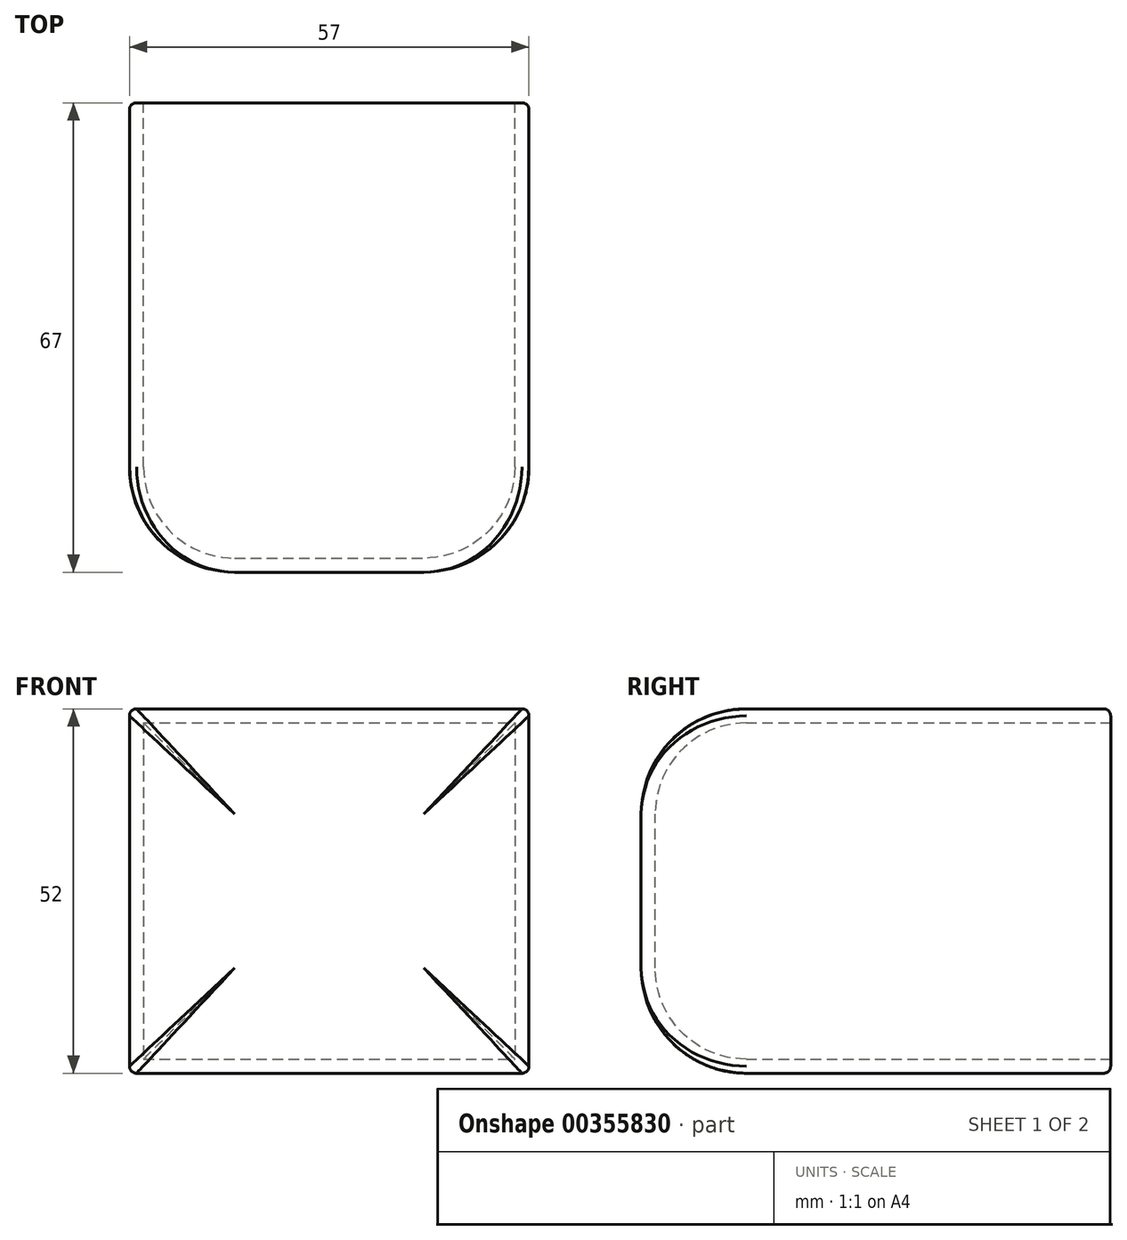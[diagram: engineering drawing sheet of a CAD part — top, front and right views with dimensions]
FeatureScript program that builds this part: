
annotation { "Feature Type Name" : "Feature", "Feature Type Description" : "" }
export const myFeature = defineFeature(function(context is Context, id is Id, definition is map)
    precondition{}
    {
        {
            var Q0;
            Q0=qCreatedBy(makeId("Front.planeOp"),FACE);
            var sketch = newSketch(context, id + "F0", { "sketchPlane" : qUnion([Q0])});
            skLineSegment(sketch, "E0.bottom", {"start": v(-28.5, 26) * mm, "end": v(28.5, 26) * mm});
            skLineSegment(sketch, "E0.top", {"start": v(-28.5, -26) * mm, "end": v(28.5, -26) * mm});
            skLineSegment(sketch, "E0.left", {"start": v(-28.5, 26) * mm, "end": v(-28.5, -26) * mm});
            skLineSegment(sketch, "E0.right", {"start": v(28.5, 26) * mm, "end": v(28.5, -26) * mm});
            skPoint(sketch, "E0.middle", {"position": v(0, 0) * mm});
            skSolve(sketch);
        }
        {
            var Q0;
            Q0=qSketchRegion(id+"F0",true);
            extrude(context, id + "F1", {"entities" : qUnion([Q0]), "depth" : 67 * mm});
        }
        {
            var Q0;
            Q0=makeQuery(id+"F1.opExtrude","CAP_FACE",FACE,{"disambiguationData":[OSD([sQuery(id+"F0.wireOp",EDGE,"E0.bottom"),sQuery(id+"F0.wireOp",EDGE,"E0.top"),sQuery(id+"F0.wireOp",EDGE,"E0.left"),sQuery(id+"F0.wireOp",EDGE,"E0.right")])],"isStart":false});
            fillet(context, id + "F2", {"entities" : qUnion([Q0]), "radius" : 15 * mm, "tangentPropagation" : true, "allowEdgeOverflow" : false});
        }
        {
            var Q0;
            Q0=makeQuery(id+"F1.opExtrude","CAP_FACE",FACE,{"disambiguationData":[OSD([sQuery(id+"F0.wireOp",EDGE,"E0.bottom"),sQuery(id+"F0.wireOp",EDGE,"E0.top"),sQuery(id+"F0.wireOp",EDGE,"E0.left"),sQuery(id+"F0.wireOp",EDGE,"E0.right")])],"isStart":true});
            shell(context, id + "F3", {"entities" : qUnion([Q0]), "thickness" : 2 * mm});
        }
        {
            var Q0;
            Q0=makeQuery(id+"F1.opExtrude","CAP_EDGE",EDGE,{"disambiguationData":[OSD([sQuery(id+"F0.wireOp",EDGE,"E0.left")])],"isStart":true});
            fillet(context, id + "F4", {"entities" : qUnion([Q0]), "radius" : 1 * mm, "tangentPropagation" : true, "allowEdgeOverflow" : false});
        }
        {
            var Q0;
            Q0=makeQuery(id+"F1.opExtrude","CAP_EDGE",EDGE,{"disambiguationData":[OSD([sQuery(id+"F0.wireOp",EDGE,"E0.right")])],"isStart":true});
            fillet(context, id + "F5", {"entities" : qUnion([Q0]), "radius" : 1 * mm, "tangentPropagation" : true, "allowEdgeOverflow" : false});
        }
        {
            var Q0;
            Q0=makeQuery(id+"F1.opExtrude","SWEPT_EDGE",EDGE,{"disambiguationData":[OSD([sQuery(id+"F0.wireOp",EDGE,"E0.bottom"),sQuery(id+"F0.wireOp",EDGE,"E0.right")])]});
            var Q1;
            Q1=makeQuery(id+"F1.opExtrude","SWEPT_EDGE",EDGE,{"disambiguationData":[OSD([sQuery(id+"F0.wireOp",EDGE,"E0.top"),sQuery(id+"F0.wireOp",EDGE,"E0.right")])]});
            var Q2;
            Q2=makeQuery(id+"F1.opExtrude","SWEPT_EDGE",EDGE,{"disambiguationData":[OSD([sQuery(id+"F0.wireOp",EDGE,"E0.bottom"),sQuery(id+"F0.wireOp",EDGE,"E0.left")])]});
            var Q3;
            Q3=makeQuery(id+"F1.opExtrude","SWEPT_EDGE",EDGE,{"disambiguationData":[OSD([sQuery(id+"F0.wireOp",EDGE,"E0.top"),sQuery(id+"F0.wireOp",EDGE,"E0.left")])]});
            fillet(context, id + "F6", {"entities" : qUnion([Q0, Q1, Q2, Q3]), "radius" : 1 * mm, "tangentPropagation" : true, "allowEdgeOverflow" : false});
        }
    });
